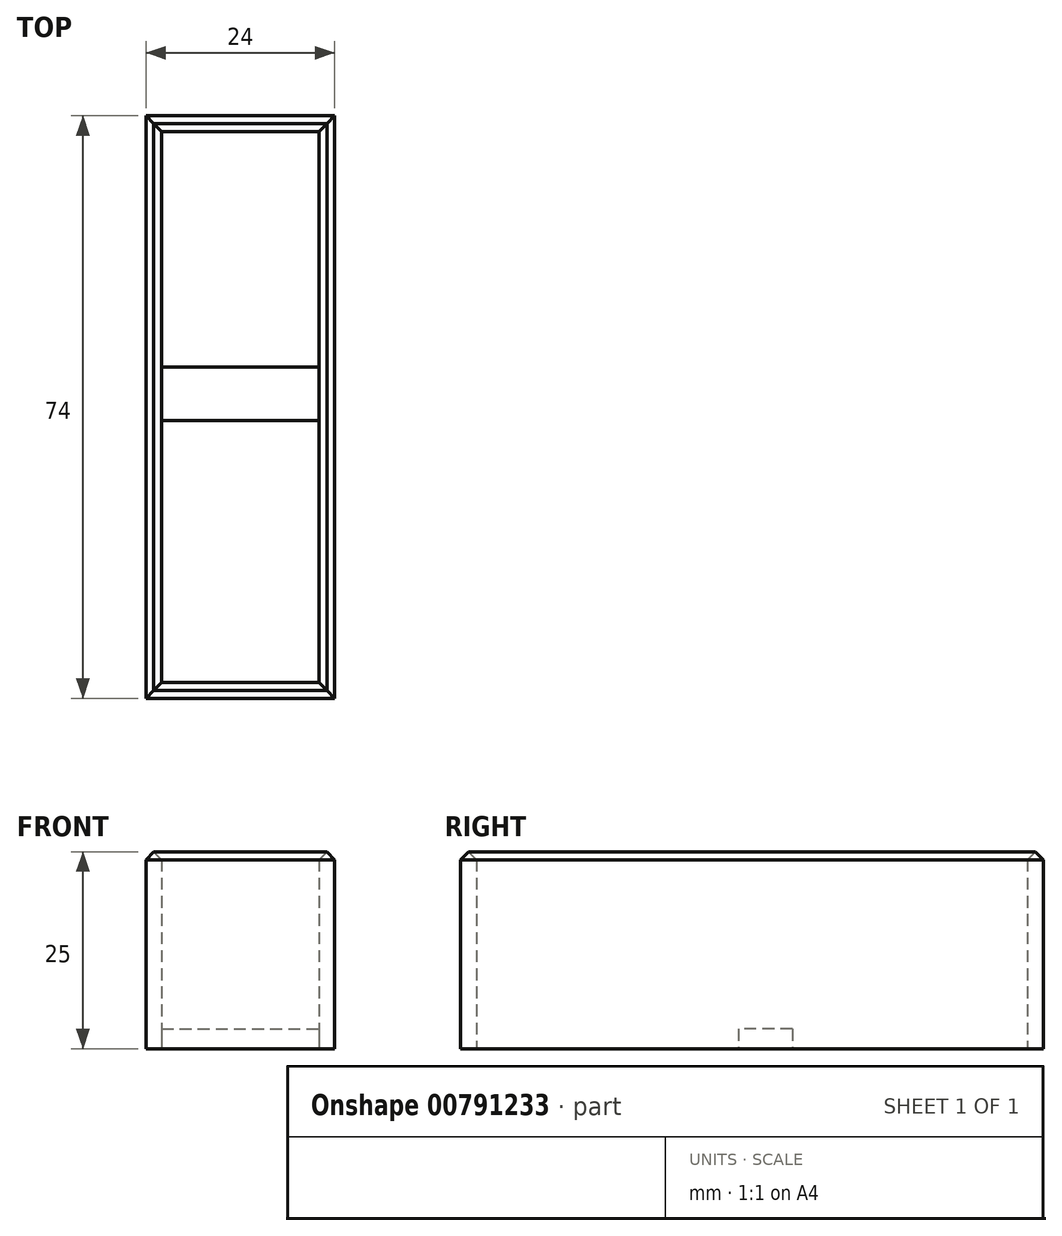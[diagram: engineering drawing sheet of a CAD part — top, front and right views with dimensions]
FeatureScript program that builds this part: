
annotation { "Feature Type Name" : "Feature", "Feature Type Description" : "" }
export const myFeature = defineFeature(function(context is Context, id is Id, definition is map)
    precondition{}
    {
        {
            var Q0;
            Q0=qCreatedBy(makeId("Top.planeOp"),FACE);
            var sketch = newSketch(context, id + "F0", { "sketchPlane" : qUnion([Q0])});
            skLineSegment(sketch, "E0.bottom", {"start": v(-12.64, 42.6) * mm, "end": v(7.36, 42.6) * mm});
            skLineSegment(sketch, "E0.top", {"start": v(-12.64, -27.4) * mm, "end": v(7.36, -27.4) * mm});
            skLineSegment(sketch, "E0.left", {"start": v(-12.64, 42.6) * mm, "end": v(-12.64, -27.4) * mm});
            skLineSegment(sketch, "E0.right", {"start": v(7.36, 42.6) * mm, "end": v(7.36, -27.4) * mm});
            skLineSegment(sketch, "E1.0", {"start": v(-14.64, 44.6) * mm, "end": v(9.36, 44.6) * mm});
            skLineSegment(sketch, "E1.1", {"start": v(-14.64, 44.6) * mm, "end": v(-14.64, -29.4) * mm});
            skLineSegment(sketch, "E1.2", {"start": v(-14.64, -29.4) * mm, "end": v(9.36, -29.4) * mm});
            skLineSegment(sketch, "E1.3", {"start": v(9.36, 44.6) * mm, "end": v(9.36, -29.4) * mm});
            skLineSegment(sketch, "E2.bottom", {"start": v(-12.64, 5.87) * mm, "end": v(7.36, 5.87) * mm});
            skLineSegment(sketch, "E2.top", {"start": v(-12.64, 12.72) * mm, "end": v(7.36, 12.72) * mm});
            skLineSegment(sketch, "E2.left", {"start": v(-12.64, 5.87) * mm, "end": v(-12.64, 12.72) * mm});
            skLineSegment(sketch, "E2.right", {"start": v(7.36, 5.87) * mm, "end": v(7.36, 12.72) * mm});
            skSolve(sketch);
        }
        {
            var Q0;
            Q0 = qSketchRegion(id + "F0", true);
            extrude(context, id + "F1", {"entities" : qUnion([Q0]), "depth" : 25 * mm, "offsetDistance" : 25 * mm});
        }
        {
            var Q0;
            Q0 = qSketchRegion(id + "F0", true);
            var Q1;
            Q1=makeQuery(id+"F0.imprint","IMPRINT",FACE,{"disambiguationData":[TD([[makeQuery(id+"F0.imprint","IMPRINT",EDGE,{"derivedFrom":sQuery(id+"F0.wireOp",EDGE,"E2.bottom")}),1.0]])]});
            extrude(context, id + "F2", {"entities" : qUnion([Q0, Q1]), "operationType" : NewBodyOperationType.ADD, "depth" : 2.5 * mm, "offsetDistance" : 25 * mm});
        }
        {
            var Q0;
            Q0=makeQuery(id+"F1.opExtrude","CAP_EDGE",EDGE,{"disambiguationData":[OSD([sQuery(id+"F0.wireOp",EDGE,"E1.2")])],"isStart":false});
            var Q1;
            Q1=makeQuery(id+"F1.opExtrude","CAP_EDGE",EDGE,{"disambiguationData":[OSD([sQuery(id+"F0.wireOp",EDGE,"E1.1")])],"isStart":false});
            var Q2;
            Q2=makeQuery(id+"F1.opExtrude","CAP_EDGE",EDGE,{"disambiguationData":[OSD([sQuery(id+"F0.wireOp",EDGE,"E1.3")])],"isStart":false});
            var Q3;
            Q3=makeQuery(id+"F1.opExtrude","CAP_EDGE",EDGE,{"disambiguationData":[OSD([sQuery(id+"F0.wireOp",EDGE,"E1.0")])],"isStart":false});
            var Q4;
            Q4=makeQuery(id+"F1.opExtrude","CAP_EDGE",EDGE,{"disambiguationData":[OSD([sQuery(id+"F0.wireOp",EDGE,"E0.bottom")])],"isStart":false});
            var Q5;
            Q5=makeQuery(id+"F1.opExtrude","CAP_EDGE",EDGE,{"disambiguationData":[OSD([sQuery(id+"F0.wireOp",EDGE,"E0.right"),sQuery(id+"F0.wireOp",EDGE,"E2.right")])],"isStart":false});
            var Q6;
            Q6=makeQuery(id+"F1.opExtrude","CAP_EDGE",EDGE,{"disambiguationData":[OSD([sQuery(id+"F0.wireOp",EDGE,"E0.left"),sQuery(id+"F0.wireOp",EDGE,"E2.left")])],"isStart":false});
            var Q7;
            Q7=makeQuery(id+"F1.opExtrude","CAP_EDGE",EDGE,{"disambiguationData":[OSD([sQuery(id+"F0.wireOp",EDGE,"E0.top")])],"isStart":false});
            chamfer(context, id + "F3", {"entities" : qUnion([Q0, Q1, Q2, Q3, Q4, Q5, Q6, Q7]), "width" : 1 * mm, "tangentPropagation" : true});
        }
    });
